# Revit family: LWFLED_R16
name_source: partatom
category: Lighting Fixtures
revit_build: Autodesk Revit 2016 (Build: 20150714_1515(x64)
units: mm (PartAtom-declared; Revit-internal decimal feet)

## family parameters
Always vertical = Yes
Cut with Voids When Loaded = No
Light Source = Yes
OmniClass Number = 23.80.70.00
OmniClass Title = Lighting
Part Type = Normal
Room Calculation Point = No
Round Connector Dimension = Use Diameter
Shared = No
Work Plane-Based = No

## types (1)
- LWFLED_R16
    AS2293 Classification = C0=N/A C90=N/A
    Catalogue Number = LWFLED
    Charging Method = Intelligent Current Limited Constant Voltage
    Color Filter = 16777215
    Construction = Polycarbonate
    Description = L10 Optimum LED weatherproof Supalite flood unit, surface mount emergency light
    Dimensions L x W x H = Main enclosure - 130mm (W) x 380mm (H) x 190mm (D)
Total height including LED Heads 510mm.
Total height including LED Heads 510mm.
    Dimming Lamp Color Temperature Shift = <None>
    IP Rating = IP65
    Lamp(s) = 2 x LED Heads (adjustable), 490lm per lamp head.
    Mounting = Surface Wall Mount (hard wired supply connection)
    Operating Mode = Non-maintained
    Operating Temperature = 0˚C to 40˚C
    Operating Voltage = 240V AC; 50Hz
    Photometric Web File = 6021_LWFLED_500mA_09092016-01_IES2002_Revised.ies
    Power Consumption = 1.0 Watts (Standby)
    Testing System = N/A - Manual test switch
    Tilt Angle = 0.00°
    Total Lumen Output = 980 lm
